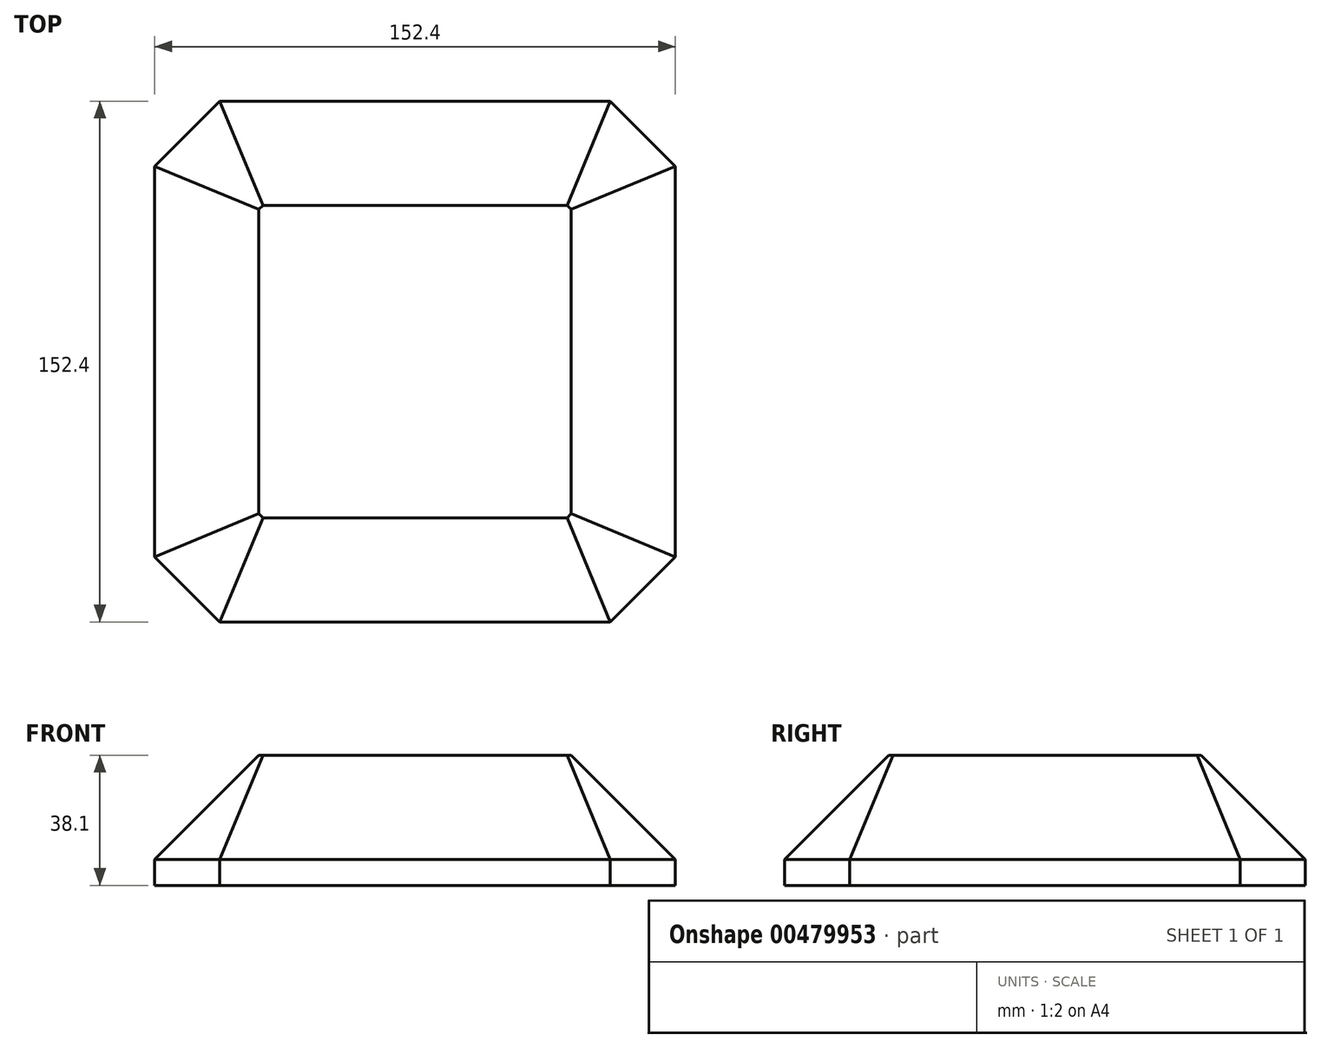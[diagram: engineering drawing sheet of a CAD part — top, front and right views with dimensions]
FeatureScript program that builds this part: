
annotation { "Feature Type Name" : "Feature", "Feature Type Description" : "" }
export const myFeature = defineFeature(function(context is Context, id is Id, definition is map)
    precondition{}
    {
        {
            var Q0;
            Q0=qCreatedBy(makeId("Top.planeOp"),FACE);
            var sketch = newSketch(context, id + "F0", { "sketchPlane" : qUnion([Q0])});
            skLineSegment(sketch, "E0.bottom", {"start": v(76.2, -76.2) * mm, "end": v(-76.2, -76.2) * mm});
            skLineSegment(sketch, "E0.top", {"start": v(76.2, 76.2) * mm, "end": v(-76.2, 76.2) * mm});
            skLineSegment(sketch, "E0.left", {"start": v(76.2, -76.2) * mm, "end": v(76.2, 76.2) * mm});
            skLineSegment(sketch, "E0.right", {"start": v(-76.2, -76.2) * mm, "end": v(-76.2, 76.2) * mm});
            skPoint(sketch, "E0.middle", {"position": v(0, 0) * mm});
            skSolve(sketch);
        }
        {
            var Q0;
            Q0 = qSketchRegion(id + "F0", true);
            extrude(context, id + "F1", {"entities" : qUnion([Q0]), "depth" : 38.1 * mm});
        }
        {
            var Q0;
            Q0=makeQuery(id+"F1.opExtrude","SWEPT_EDGE",EDGE,{"disambiguationData":[OSD([sQuery(id+"F0.wireOp",EDGE,"E0.bottom"),sQuery(id+"F0.wireOp",EDGE,"E0.right")])]});
            var Q1;
            Q1=makeQuery(id+"F1.opExtrude","SWEPT_EDGE",EDGE,{"disambiguationData":[OSD([sQuery(id+"F0.wireOp",EDGE,"E0.bottom"),sQuery(id+"F0.wireOp",EDGE,"E0.left")])]});
            var Q2;
            Q2=makeQuery(id+"F1.opExtrude","SWEPT_EDGE",EDGE,{"disambiguationData":[OSD([sQuery(id+"F0.wireOp",EDGE,"E0.top"),sQuery(id+"F0.wireOp",EDGE,"E0.left")])]});
            var Q3;
            Q3=makeQuery(id+"F1.opExtrude","SWEPT_EDGE",EDGE,{"disambiguationData":[OSD([sQuery(id+"F0.wireOp",EDGE,"E0.top"),sQuery(id+"F0.wireOp",EDGE,"E0.right")])]});
            chamfer(context, id + "F2", {"entities" : qUnion([Q0, Q1, Q2, Q3]), "width" : 19.05 * mm, "tangentPropagation" : true});
        }
        {
            var Q0;
            Q0=makeQuery(id+"F1.opExtrude","CAP_EDGE",EDGE,{"disambiguationData":[OSD([sQuery(id+"F0.wireOp",EDGE,"E0.bottom")])],"isStart":false});
            var Q1;
            Q1=makeQuery(id+"F1.opExtrude","CAP_EDGE",EDGE,{"disambiguationData":[OSD([sQuery(id+"F0.wireOp",EDGE,"E0.right")])],"isStart":false});
            var Q2;
            Q2=makeQuery(id+"F1.opExtrude","CAP_EDGE",EDGE,{"disambiguationData":[OSD([sQuery(id+"F0.wireOp",EDGE,"E0.top")])],"isStart":false});
            var Q3;
            Q3=makeQuery(id+"F1.opExtrude","CAP_EDGE",EDGE,{"disambiguationData":[OSD([sQuery(id+"F0.wireOp",EDGE,"E0.left")])],"isStart":false});
            var Q4;
            {var subQ0=sQuery(id+"F0.wireOp",EDGE,"E0.left");var subQ1=sQuery(id+"F0.wireOp",EDGE,"E0.bottom");Q4=makeQuery(id+"F2.opChamfer","BLEND_EDGE",EDGE,{"blendedFrom":[makeQuery(id+"F1.opExtrude","SWEPT_EDGE",EDGE,{"disambiguationData":[OSD([subQ1,subQ0])]}),makeQuery(id+"F1.opExtrude","CAP_FACE",FACE,{"disambiguationData":[OSD([subQ1,sQuery(id+"F0.wireOp",EDGE,"E0.top"),subQ0,sQuery(id+"F0.wireOp",EDGE,"E0.right")])],"isStart":false})],"blendedInto":[makeQuery(id+"F1.opExtrude","CAP_FACE",FACE,{"disambiguationData":[OSD([subQ1,sQuery(id+"F0.wireOp",EDGE,"E0.top"),subQ0,sQuery(id+"F0.wireOp",EDGE,"E0.right")])],"isStart":false})]});}
            var Q5;
            {var subQ0=sQuery(id+"F0.wireOp",EDGE,"E0.left");var subQ1=sQuery(id+"F0.wireOp",EDGE,"E0.top");Q5=makeQuery(id+"F2.opChamfer","BLEND_EDGE",EDGE,{"blendedFrom":[makeQuery(id+"F1.opExtrude","SWEPT_EDGE",EDGE,{"disambiguationData":[OSD([subQ1,subQ0])]}),makeQuery(id+"F1.opExtrude","CAP_FACE",FACE,{"disambiguationData":[OSD([sQuery(id+"F0.wireOp",EDGE,"E0.bottom"),subQ1,subQ0,sQuery(id+"F0.wireOp",EDGE,"E0.right")])],"isStart":false})],"blendedInto":[makeQuery(id+"F1.opExtrude","CAP_FACE",FACE,{"disambiguationData":[OSD([sQuery(id+"F0.wireOp",EDGE,"E0.bottom"),subQ1,subQ0,sQuery(id+"F0.wireOp",EDGE,"E0.right")])],"isStart":false})]});}
            var Q6;
            {var subQ0=sQuery(id+"F0.wireOp",EDGE,"E0.right");var subQ1=sQuery(id+"F0.wireOp",EDGE,"E0.top");Q6=makeQuery(id+"F2.opChamfer","BLEND_EDGE",EDGE,{"blendedFrom":[makeQuery(id+"F1.opExtrude","SWEPT_EDGE",EDGE,{"disambiguationData":[OSD([subQ1,subQ0])]}),makeQuery(id+"F1.opExtrude","CAP_FACE",FACE,{"disambiguationData":[OSD([sQuery(id+"F0.wireOp",EDGE,"E0.bottom"),subQ1,sQuery(id+"F0.wireOp",EDGE,"E0.left"),subQ0])],"isStart":false})],"blendedInto":[makeQuery(id+"F1.opExtrude","CAP_FACE",FACE,{"disambiguationData":[OSD([sQuery(id+"F0.wireOp",EDGE,"E0.bottom"),subQ1,sQuery(id+"F0.wireOp",EDGE,"E0.left"),subQ0])],"isStart":false})]});}
            var Q7;
            {var subQ0=sQuery(id+"F0.wireOp",EDGE,"E0.right");var subQ1=sQuery(id+"F0.wireOp",EDGE,"E0.bottom");Q7=makeQuery(id+"F2.opChamfer","BLEND_EDGE",EDGE,{"blendedFrom":[makeQuery(id+"F1.opExtrude","SWEPT_EDGE",EDGE,{"disambiguationData":[OSD([subQ1,subQ0])]}),makeQuery(id+"F1.opExtrude","CAP_FACE",FACE,{"disambiguationData":[OSD([subQ1,sQuery(id+"F0.wireOp",EDGE,"E0.top"),sQuery(id+"F0.wireOp",EDGE,"E0.left"),subQ0])],"isStart":false})],"blendedInto":[makeQuery(id+"F1.opExtrude","CAP_FACE",FACE,{"disambiguationData":[OSD([subQ1,sQuery(id+"F0.wireOp",EDGE,"E0.top"),sQuery(id+"F0.wireOp",EDGE,"E0.left"),subQ0])],"isStart":false})]});}
            chamfer(context, id + "F3", {"entities" : qUnion([Q0, Q1, Q2, Q3, Q4, Q5, Q6, Q7]), "width" : 30.48 * mm, "tangentPropagation" : true});
        }
    });
